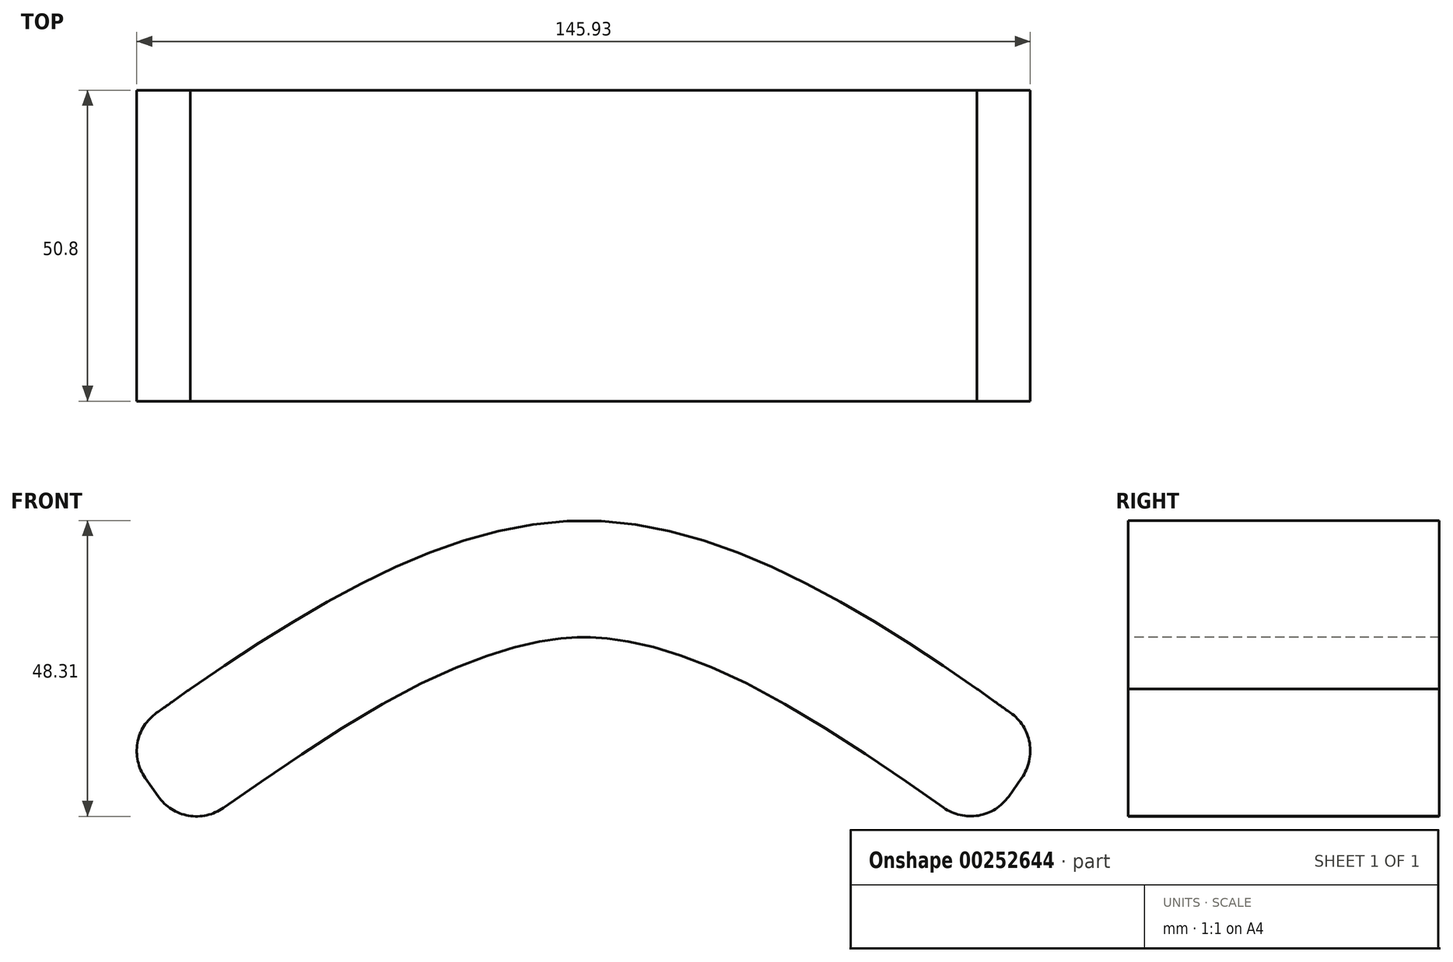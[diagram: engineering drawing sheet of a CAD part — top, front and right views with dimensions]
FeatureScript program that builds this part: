
annotation { "Feature Type Name" : "Feature", "Feature Type Description" : "" }
export const myFeature = defineFeature(function(context is Context, id is Id, definition is map)
    precondition{}
    {
        {
            var Q0;
            Q0=qCreatedBy(makeId("Front.planeOp"),FACE);
            var sketch = newSketch(context, id + "F0", { "sketchPlane" : qUnion([Q0])});
            skFitSpline(sketch, "E0", {"points": [v(-76.16, 0) * mm, v(0, 35.7) * mm, v(75.9, 0) * mm], "startDerivative": vector(152.28, 107.1) * mm, "endDerivative": vector(151.81, -107.15) * mm});
            skFitSpline(sketch, "E1.0", {"points": [v(-76.14, -0.02) * mm, v(-63.45, 8.9) * mm, v(-44.42, 22.29) * mm, v(-19.06, 33.45) * mm, v(-0.05, 36.8) * mm, v(18.94, 33.46) * mm, v(44.25, 22.3) * mm, v(63.22, 8.9) * mm, v(75.88, -0.02) * mm]});
            skFitSpline(sketch, "E2.0", {"points": [v(-65.18, -15.6) * mm, v(-62, -13.37) * mm, v(-55.74, -8.96) * mm, v(-46.57, -2.72) * mm, v(-37.68, 2.94) * mm, v(-29.12, 7.83) * mm, v(-22.33, 11.1) * mm, v(-17.16, 13.18) * mm, v(-13.42, 14.45) * mm, v(-9.84, 15.44) * mm, v(-7, 16.01) * mm, v(-4.79, 16.34) * mm, v(-3.17, 16.5) * mm, v(-1.86, 16.6) * mm, v(-0.82, 16.63) * mm, v(-0.05, 16.63) * mm, v(0.72, 16.63) * mm, v(1.76, 16.6) * mm, v(3.07, 16.5) * mm, v(4.69, 16.34) * mm, v(6.89, 16.02) * mm, v(9.73, 15.44) * mm, v(13.3, 14.46) * mm, v(17.02, 13.2) * mm, v(22.17, 11.12) * mm, v(28.94, 7.85) * mm, v(37.48, 2.97) * mm, v(46.34, -2.7) * mm, v(55.48, -8.94) * mm, v(61.73, -13.35) * mm, v(64.89, -15.59) * mm]});
            skLineSegment(sketch, "E3", {"start": v(-76.14, -0.02) * mm, "end": v(-65.18, -15.6) * mm});
            skLineSegment(sketch, "E4", {"start": v(64.89, -15.59) * mm, "end": v(75.9, 0) * mm});
            skSolve(sketch);
        }
        {
            var Q0;
            {var subQ0=sQuery(id+"F0.wireOp",EDGE,"E1.0");Q0=makeQuery(id+"F0.imprint","IMPRINT",FACE,{"disambiguationData":[TD([[makeQuery(id+"F0.imprint","IMPRINT",EDGE,{"derivedFrom":subQ0}),-1.0]])]});}
            extrude(context, id + "F1", {"entities" : qUnion([Q0]), "depth" : 50.8 * mm});
        }
        {
            var Q0;
            Q0=makeQuery(id+"F1.opExtrude","SWEPT_EDGE",EDGE,{"disambiguationData":[OSD([sQuery(id+"F0.wireOp",EDGE,"E2.0"),sQuery(id+"F0.wireOp",EDGE,"E4")])]});
            var Q1;
            Q1=makeQuery(id+"F1.opExtrude","SWEPT_EDGE",EDGE,{"disambiguationData":[OSD([sQuery(id+"F0.wireOp",EDGE,"E1.0"),sQuery(id+"F0.wireOp",EDGE,"E4")])]});
            var Q2;
            Q2=makeQuery(id+"F1.opExtrude","SWEPT_EDGE",EDGE,{"disambiguationData":[OSD([sQuery(id+"F0.wireOp",EDGE,"E2.0"),sQuery(id+"F0.wireOp",EDGE,"E3")])]});
            var Q3;
            Q3=makeQuery(id+"F1.opExtrude","SWEPT_EDGE",EDGE,{"disambiguationData":[OSD([sQuery(id+"F0.wireOp",EDGE,"E1.0"),sQuery(id+"F0.wireOp",EDGE,"E3")])]});
            fillet(context, id + "F2", {"entities" : qUnion([Q0, Q1, Q2, Q3]), "radius" : 7.62 * mm, "tangentPropagation" : true, "allowEdgeOverflow" : false});
        }
    });
